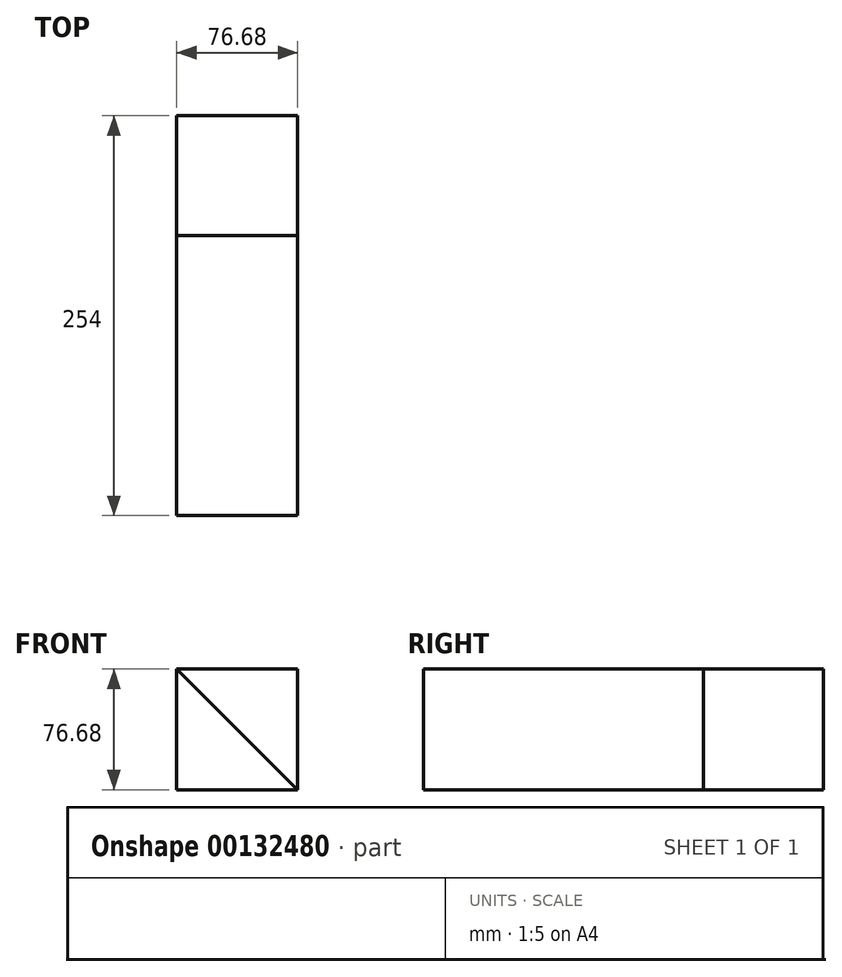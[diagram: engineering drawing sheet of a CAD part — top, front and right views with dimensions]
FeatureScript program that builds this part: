
annotation { "Feature Type Name" : "Feature", "Feature Type Description" : "" }
export const myFeature = defineFeature(function(context is Context, id is Id, definition is map)
    precondition{}
    {
        {
            var Q0;
            Q0=qCreatedBy(makeId("Front.planeOp"),FACE);
            var sketch = newSketch(context, id + "F0", { "sketchPlane" : qUnion([Q0])});
            skLineSegment(sketch, "E0", {"start": v(0, 0) * mm, "end": v(76.68, 0) * mm});
            skLineSegment(sketch, "E1", {"start": v(76.68, 0) * mm, "end": v(76.68, 76.68) * mm});
            skLineSegment(sketch, "E2", {"start": v(76.68, 76.68) * mm, "end": v(0, 76.68) * mm});
            skLineSegment(sketch, "E3", {"start": v(0, 76.68) * mm, "end": v(0, 0) * mm});
            skSolve(sketch);
        }
        {
            var Q0;
            Q0=makeQuery(id+"F0.imprint","IMPRINT",FACE,{"disambiguationData":[TD([[makeQuery(id+"F0.imprint","IMPRINT",EDGE,{"derivedFrom":sQuery(id+"F0.wireOp",EDGE,"E0")}),1.0]])]});
            extrude(context, id + "F1", {"entities" : qUnion([Q0]), "depth" : 76.2 * mm});
        }
        {
            var Q0;
            Q0=makeQuery(id+"F1.opExtrude","CAP_FACE",FACE,{"disambiguationData":[OSD([sQuery(id+"F0.wireOp",EDGE,"E0"),sQuery(id+"F0.wireOp",EDGE,"E1"),sQuery(id+"F0.wireOp",EDGE,"E2"),sQuery(id+"F0.wireOp",EDGE,"E3")])],"isStart":false});
            var sketch = newSketch(context, id + "F2", { "sketchPlane" : qUnion([Q0])});
            skLineSegment(sketch, "E4", {"start": v(0, 76.68) * mm, "end": v(76.68, 76.68) * mm});
            skLineSegment(sketch, "E5", {"start": v(76.68, 76.68) * mm, "end": v(76.68, 0) * mm});
            skLineSegment(sketch, "E6", {"start": v(76.68, 0) * mm, "end": v(0, 76.68) * mm});
            skSolve(sketch);
        }
        {
            var Q0;
            Q0=makeQuery(id+"F2.imprint","IMPRINT",FACE,{"disambiguationData":[TD([[makeQuery(id+"F2.imprint","IMPRINT",EDGE,{"derivedFrom":sQuery(id+"F2.wireOp",EDGE,"E6")}),1.0]])]});
            extrude(context, id + "F3", {"entities" : qUnion([Q0]), "operationType" : NewBodyOperationType.ADD, "depth" : 177.8 * mm});
        }
    });
